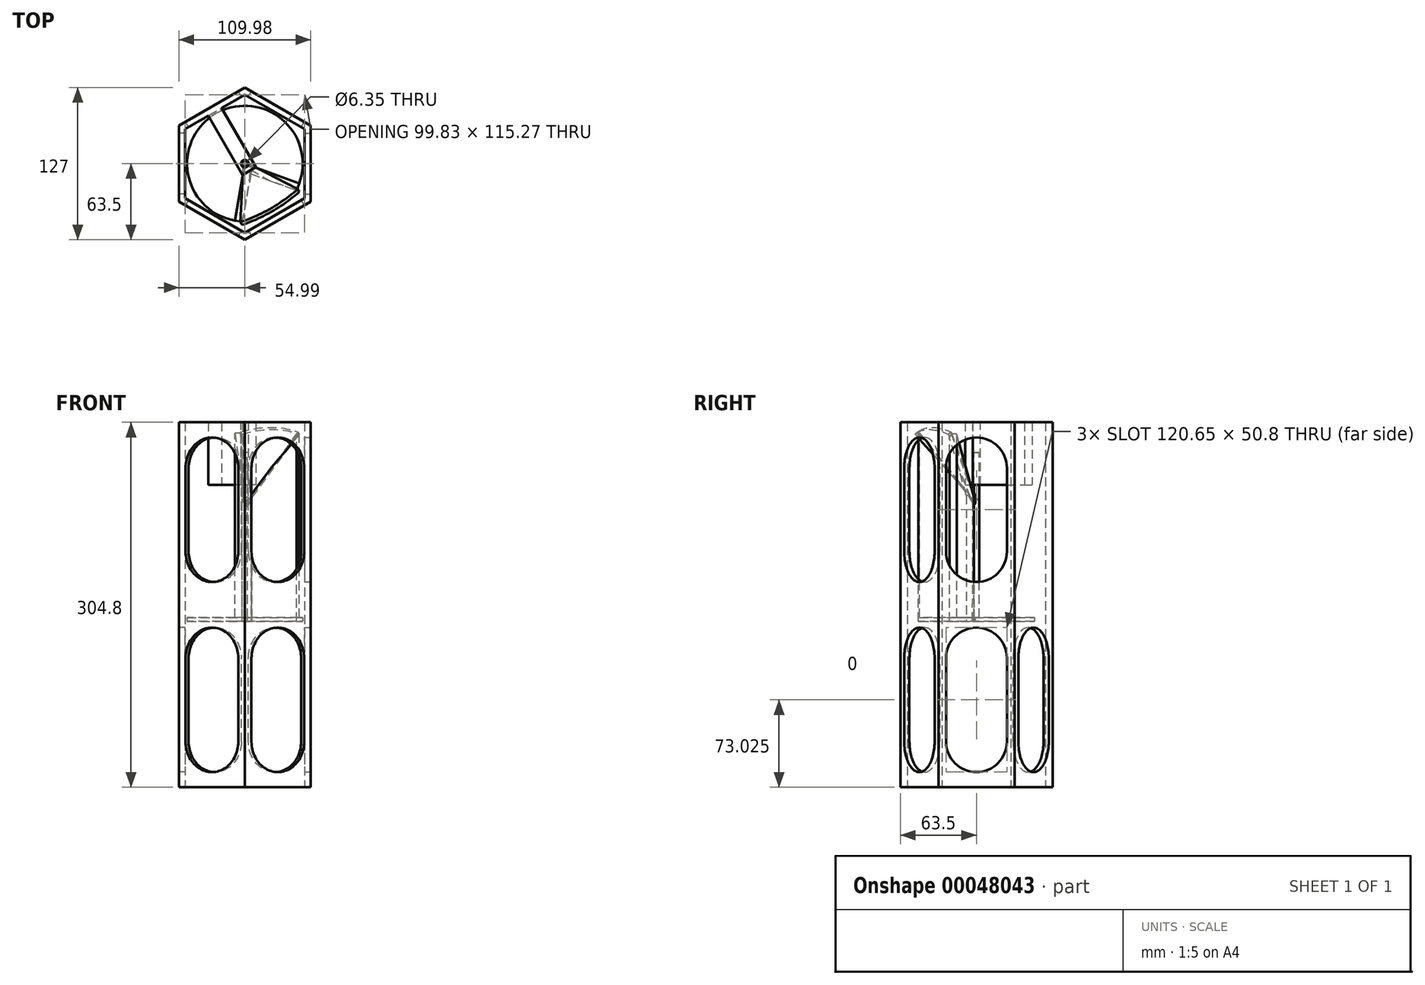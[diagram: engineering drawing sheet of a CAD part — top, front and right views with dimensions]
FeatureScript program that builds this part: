
annotation { "Feature Type Name" : "Feature", "Feature Type Description" : "" }
export const myFeature = defineFeature(function(context is Context, id is Id, definition is map)
    precondition{}
    {
        {
            var Q0;
            Q0=qCreatedBy(makeId("Top.planeOp"),FACE);
            var sketch = newSketch(context, id + "F0", { "sketchPlane" : qUnion([Q0])});
            skLineSegment(sketch, "E0", {"start": v(-55, 0) * mm, "end": v(-55, 31.75) * mm});
            skLineSegment(sketch, "E1", {"start": v(-55, 31.75) * mm, "end": v(0, 63.5) * mm});
            skLineSegment(sketch, "E2", {"start": v(0, 63.5) * mm, "end": v(55, 31.75) * mm});
            skLineSegment(sketch, "E3", {"start": v(55, 31.75) * mm, "end": v(55, 0) * mm});
            skLineSegment(sketch, "E4", {"start": v(55, 0) * mm, "end": v(55, -31.75) * mm});
            skLineSegment(sketch, "E5", {"start": v(55, -31.75) * mm, "end": v(0, -63.5) * mm});
            skLineSegment(sketch, "E6", {"start": v(0, -63.5) * mm, "end": v(-55, -31.75) * mm});
            skLineSegment(sketch, "E7", {"start": v(-55, -31.75) * mm, "end": v(-55, 0) * mm});
            skLineSegment(sketch, "E8.0", {"start": v(-49.91, 0) * mm, "end": v(-49.91, 28.82) * mm});
            skLineSegment(sketch, "E8.1", {"start": v(-49.91, -28.82) * mm, "end": v(-49.91, 0) * mm});
            skLineSegment(sketch, "E8.2", {"start": v(-49.91, 28.82) * mm, "end": v(0, 57.63) * mm});
            skLineSegment(sketch, "E8.3", {"start": v(0, -57.63) * mm, "end": v(-49.91, -28.82) * mm});
            skLineSegment(sketch, "E8.4", {"start": v(0, 57.63) * mm, "end": v(49.91, 28.82) * mm});
            skLineSegment(sketch, "E8.5", {"start": v(49.91, 28.82) * mm, "end": v(49.91, 0) * mm});
            skLineSegment(sketch, "E8.6", {"start": v(49.91, 0) * mm, "end": v(49.91, -28.82) * mm});
            skLineSegment(sketch, "E8.7", {"start": v(49.91, -28.82) * mm, "end": v(0, -57.63) * mm});
            skSolve(sketch);
        }
        {
            var Q0;
            Q0 = qSketchRegion(id + "F0", true);
            extrude(context, id + "F1", {"entities" : qUnion([Q0]), "depth" : 304.8 * mm});
        }
        {
            var Q0;
            Q0=makeQuery(id+"F1.opExtrude","SWEPT_FACE",FACE,{"disambiguationData":[OSD([sQuery(id+"F0.wireOp",EDGE,"E1")])]});
            var sketch = newSketch(context, id + "F2", { "sketchPlane" : qUnion([Q0])});
            skLineSegment(sketch, "E9", {"start": v(31.75, 152.4) * mm, "end": v(-31.75, 152.4) * mm, "construction": true});
            skSolve(sketch);
        }
        {
            var Q0;
            Q0=sQuery(id+"F2.wireOp",VERTEX,"E9.start");
            var Q1;
            Q1=sQuery(id+"F2.wireOp",VERTEX,"E9.end");
            var Q2;
            Q2=makeQuery(id+"F1.opExtrude","CAP_VERTEX",VERTEX,{"disambiguationData":[OSD([sQuery(id+"F0.wireOp",EDGE,"E8.3"),sQuery(id+"F0.wireOp",EDGE,"E8.7")])],"isStart":false});
            cPlane(context, id + "F3", {"entities" : qUnion([Q0, Q1, Q2]), "cplaneType" : CPlaneType.THREE_POINT, "offset" : 152.4 * mm, "width" : 152.4 * mm, "height" : 152.4 * mm});
        }
        {
            var Q0;
            Q0=makeQuery(id+"F1.opExtrude","CAP_VERTEX",VERTEX,{"disambiguationData":[OSD([sQuery(id+"F0.wireOp",EDGE,"E8.1"),sQuery(id+"F0.wireOp",EDGE,"E8.3")])],"isStart":false});
            var Q1;
            Q1=makeQuery(id+"F1.opExtrude","CAP_VERTEX",VERTEX,{"disambiguationData":[OSD([sQuery(id+"F0.wireOp",EDGE,"E8.4"),sQuery(id+"F0.wireOp",EDGE,"E8.5")])],"isStart":false});
            var Q2;
            Q2=makeQuery(id+"F1.opExtrude","CAP_VERTEX",VERTEX,{"disambiguationData":[OSD([sQuery(id+"F0.wireOp",EDGE,"E8.4"),sQuery(id+"F0.wireOp",EDGE,"E8.5")])],"isStart":true});
            cPlane(context, id + "F4", {"entities" : qUnion([Q0, Q1, Q2]), "cplaneType" : CPlaneType.THREE_POINT, "offset" : 152.4 * mm, "width" : 152.4 * mm, "height" : 152.4 * mm});
        }
        {
            var Q0;
            Q0=makeQuery(id+"F1.opExtrude","CAP_VERTEX",VERTEX,{"disambiguationData":[OSD([sQuery(id+"F0.wireOp",EDGE,"E8.0"),sQuery(id+"F0.wireOp",EDGE,"E8.2")])],"isStart":false});
            var Q1;
            Q1=makeQuery(id+"F1.opExtrude","CAP_VERTEX",VERTEX,{"disambiguationData":[OSD([sQuery(id+"F0.wireOp",EDGE,"E8.0"),sQuery(id+"F0.wireOp",EDGE,"E8.2")])],"isStart":true});
            var Q2;
            Q2=makeQuery(id+"F1.opExtrude","CAP_VERTEX",VERTEX,{"disambiguationData":[OSD([sQuery(id+"F0.wireOp",EDGE,"E8.6"),sQuery(id+"F0.wireOp",EDGE,"E8.7")])],"isStart":false});
            cPlane(context, id + "F5", {"entities" : qUnion([Q0, Q1, Q2]), "cplaneType" : CPlaneType.THREE_POINT, "offset" : 152.4 * mm, "width" : 152.4 * mm, "height" : 152.4 * mm});
        }
        {
            var Q0;
            Q0=qCreatedBy(id+"F3.planeOp",FACE);
            var sketch = newSketch(context, id + "F6", { "sketchPlane" : qUnion([Q0])});
            skLineSegment(sketch, "E10", {"start": v(-59.53, 181.84) * mm, "end": v(8.15, 204) * mm, "construction": true});
            skArc(sketch, "E11", {"start": v(-56.89, 262.57) * mm, "mid": v(-84.66, 258.6) * mm, "end": v(-109.4, 245.38) * mm});
            skLineSegment(sketch, "E12", {"start": v(-109.4, 245.38) * mm, "end": v(-59.53, 181.84) * mm});
            skLineSegment(sketch, "E13", {"start": v(-56.89, 262.57) * mm, "end": v(-59.53, 181.84) * mm});
            skLineSegment(sketch, "E14", {"start": v(-59.53, 181.84) * mm, "end": v(-95.11, 290.54) * mm, "construction": true});
            skSolve(sketch);
        }
        {
            var Q0;
            Q0 = qSketchRegion(id + "F6", true);
            extrude(context, id + "F7", {"entities" : qUnion([Q0]), "operationType" : NewBodyOperationType.ADD, "depth" : 3.17 * mm});
        }
        {
            var Q0;
            Q0=makeQuery(id+"F1.opExtrude","SWEPT_FACE",FACE,{"disambiguationData":[OSD([sQuery(id+"F0.wireOp",EDGE,"E8.2")])]});
            var sketch = newSketch(context, id + "F8", { "sketchPlane" : qUnion([Q0])});
            skLineSegment(sketch, "E15.bottom", {"start": v(-6.56, 304.8) * mm, "end": v(6.56, 304.8) * mm});
            skLineSegment(sketch, "E15.top", {"start": v(-6.56, 252.42) * mm, "end": v(6.56, 252.42) * mm});
            skLineSegment(sketch, "E15.left", {"start": v(-6.56, 304.8) * mm, "end": v(-6.56, 252.42) * mm});
            skLineSegment(sketch, "E15.right", {"start": v(6.56, 304.8) * mm, "end": v(6.56, 252.42) * mm});
            skLineSegment(sketch, "E16", {"start": v(0, 304.8) * mm, "end": v(0, 226.31) * mm, "construction": true});
            skPoint(sketch, "E16.endSnap0", {"position": v(0, 304.8) * mm});
            skSolve(sketch);
        }
        {
            var Q0;
            Q0 = qSketchRegion(id + "F8", true);
            extrude(context, id + "F9", {"entities" : qUnion([Q0]), "operationType" : NewBodyOperationType.ADD, "depth" : 57.15 * mm});
        }
        {
            var Q0;
            Q0=makeQuery(id+"F9.boolean.opBoolean","MERGE",FACE,{"derivedFrom":[makeQuery(id+"F1.opExtrude","CAP_FACE",FACE,{"disambiguationData":[OSD([sQuery(id+"F0.wireOp",EDGE,"E0"),sQuery(id+"F0.wireOp",EDGE,"E1"),sQuery(id+"F0.wireOp",EDGE,"E2"),sQuery(id+"F0.wireOp",EDGE,"E3"),sQuery(id+"F0.wireOp",EDGE,"E4"),sQuery(id+"F0.wireOp",EDGE,"E5"),sQuery(id+"F0.wireOp",EDGE,"E6"),sQuery(id+"F0.wireOp",EDGE,"E7"),sQuery(id+"F0.wireOp",EDGE,"E8.0"),sQuery(id+"F0.wireOp",EDGE,"E8.1"),sQuery(id+"F0.wireOp",EDGE,"E8.2"),sQuery(id+"F0.wireOp",EDGE,"E8.3"),sQuery(id+"F0.wireOp",EDGE,"E8.4"),sQuery(id+"F0.wireOp",EDGE,"E8.5"),sQuery(id+"F0.wireOp",EDGE,"E8.6"),sQuery(id+"F0.wireOp",EDGE,"E8.7")])],"isStart":false}),makeQuery(id+"F9.opExtrude","SWEPT_FACE",FACE,{"disambiguationData":[OSD([sQuery(id+"F8.wireOp",EDGE,"E15.bottom")])]})]});
            var sketch = newSketch(context, id + "F10", { "sketchPlane" : qUnion([Q0])});
            skCircle(sketch, "E17", {"center": v(0, 0) * mm, "radius": 3.18 * mm});
            skSolve(sketch);
        }
        {
            var Q0;
            Q0 = qSketchRegion(id + "F10", true);
            extrude(context, id + "F11", {"entities" : qUnion([Q0]), "operationType" : NewBodyOperationType.REMOVE, "endBound" : BoundingType.THROUGH_ALL, "oppositeDirection" : true, "depth" : 25.4 * mm});
        }
        {
            var Q0;
            Q0=makeQuery(id+"F9.boolean.opBoolean","MERGE",FACE,{"derivedFrom":[makeQuery(id+"F1.opExtrude","CAP_FACE",FACE,{"disambiguationData":[OSD([sQuery(id+"F0.wireOp",EDGE,"E0"),sQuery(id+"F0.wireOp",EDGE,"E1"),sQuery(id+"F0.wireOp",EDGE,"E2"),sQuery(id+"F0.wireOp",EDGE,"E3"),sQuery(id+"F0.wireOp",EDGE,"E4"),sQuery(id+"F0.wireOp",EDGE,"E5"),sQuery(id+"F0.wireOp",EDGE,"E6"),sQuery(id+"F0.wireOp",EDGE,"E7"),sQuery(id+"F0.wireOp",EDGE,"E8.0"),sQuery(id+"F0.wireOp",EDGE,"E8.1"),sQuery(id+"F0.wireOp",EDGE,"E8.2"),sQuery(id+"F0.wireOp",EDGE,"E8.3"),sQuery(id+"F0.wireOp",EDGE,"E8.4"),sQuery(id+"F0.wireOp",EDGE,"E8.5"),sQuery(id+"F0.wireOp",EDGE,"E8.6"),sQuery(id+"F0.wireOp",EDGE,"E8.7")])],"isStart":false}),makeQuery(id+"F9.opExtrude","SWEPT_FACE",FACE,{"disambiguationData":[OSD([sQuery(id+"F8.wireOp",EDGE,"E15.bottom")])]})]});
            var sketch = newSketch(context, id + "F12", { "sketchPlane" : qUnion([Q0])});
            skCircle(sketch, "E18", {"center": v(0, 0) * mm, "radius": 2.24 * mm});
            skSolve(sketch);
        }
        {
            var Q0;
            Q0 = qSketchRegion(id + "F12", true);
            extrude(context, id + "F13", {"entities" : qUnion([Q0]), "operationType" : NewBodyOperationType.ADD, "oppositeDirection" : true, "depth" : 166.25 * mm, "hasSecondDirection" : true, "secondDirectionOppositeDirection" : true, "secondDirectionDepth" : 25.4 * mm});
        }
        {
            var Q0;
            Q0=makeQuery(id+"F1.opExtrude","SWEPT_FACE",FACE,{"disambiguationData":[OSD([sQuery(id+"F0.wireOp",EDGE,"E3"),sQuery(id+"F0.wireOp",EDGE,"E4")])]});
            var sketch = newSketch(context, id + "F14", { "sketchPlane" : qUnion([Q0])});
            skLineSegment(sketch, "E19", {"start": v(-25.4, 266.7) * mm, "end": v(-25.4, 196.85) * mm});
            skLineSegment(sketch, "E20", {"start": v(25.4, 266.7) * mm, "end": v(25.4, 196.85) * mm});
            skArc(sketch, "E21", {"start": v(-25.4, 266.7) * mm, "mid": v(0, 292.1) * mm, "end": v(25.4, 266.7) * mm});
            skArc(sketch, "E22", {"start": v(-25.4, 196.85) * mm, "mid": v(0, 171.45) * mm, "end": v(25.4, 196.85) * mm});
            skLineSegment(sketch, "E23", {"start": v(0, 304.8) * mm, "end": v(0, 141.13) * mm, "construction": true});
            skPoint(sketch, "E23.endSnap0", {"position": v(0, 304.8) * mm});
            skLineSegment(sketch, "E24", {"start": v(-25.4, 107.95) * mm, "end": v(-25.4, 38.1) * mm});
            skArc(sketch, "E25", {"start": v(-25.4, 107.95) * mm, "mid": v(0, 133.35) * mm, "end": v(25.4, 107.95) * mm});
            skLineSegment(sketch, "E26", {"start": v(25.4, 107.95) * mm, "end": v(25.4, 38.1) * mm});
            skLineSegment(sketch, "E27", {"start": v(0, 160.02) * mm, "end": v(0, 0) * mm, "construction": true});
            skArc(sketch, "E28", {"start": v(-25.4, 38.1) * mm, "mid": v(0, 12.7) * mm, "end": v(25.4, 38.1) * mm});
            skSolve(sketch);
        }
        {
            var Q0;
            Q0 = qSketchRegion(id + "F14", true);
            extrude(context, id + "F15", {"entities" : qUnion([Q0]), "operationType" : NewBodyOperationType.REMOVE, "endBound" : BoundingType.UP_TO_NEXT, "oppositeDirection" : true, "depth" : 25.4 * mm});
        }
        {
            var Q0;
            Q0=makeQuery(id+"F1.opExtrude","SWEPT_FACE",FACE,{"disambiguationData":[OSD([sQuery(id+"F0.wireOp",EDGE,"E5")])]});
            var sketch = newSketch(context, id + "F16", { "sketchPlane" : qUnion([Q0])});
            skLineSegment(sketch, "E29", {"start": v(-25.4, 266.7) * mm, "end": v(-25.4, 196.85) * mm});
            skLineSegment(sketch, "E30", {"start": v(25.4, 266.7) * mm, "end": v(25.4, 196.85) * mm});
            skArc(sketch, "E31", {"start": v(-25.4, 196.85) * mm, "mid": v(0, 171.45) * mm, "end": v(25.4, 196.85) * mm});
            skArc(sketch, "E32", {"start": v(-25.4, 266.7) * mm, "mid": v(0, 292.1) * mm, "end": v(25.4, 266.7) * mm});
            skLineSegment(sketch, "E33", {"start": v(0, 304.8) * mm, "end": v(0, 180.72) * mm, "construction": true});
            skLineSegment(sketch, "E34", {"start": v(25.4, 107.95) * mm, "end": v(25.4, 38.1) * mm});
            skLineSegment(sketch, "E35", {"start": v(-25.4, 107.95) * mm, "end": v(-25.4, 38.1) * mm});
            skArc(sketch, "E36", {"start": v(-25.4, 38.1) * mm, "mid": v(0, 12.7) * mm, "end": v(25.4, 38.1) * mm});
            skArc(sketch, "E37", {"start": v(-25.4, 107.95) * mm, "mid": v(0, 133.35) * mm, "end": v(25.4, 107.95) * mm});
            skLineSegment(sketch, "E38", {"start": v(0, 138.62) * mm, "end": v(0, 0) * mm, "construction": true});
            skSolve(sketch);
        }
        {
            var Q0;
            Q0 = qSketchRegion(id + "F16", true);
            extrude(context, id + "F17", {"entities" : qUnion([Q0]), "operationType" : NewBodyOperationType.REMOVE, "endBound" : BoundingType.UP_TO_NEXT, "oppositeDirection" : true, "depth" : 25.4 * mm});
        }
        {
            var Q0;
            Q0=makeQuery(id+"F1.opExtrude","SWEPT_FACE",FACE,{"disambiguationData":[OSD([sQuery(id+"F0.wireOp",EDGE,"E6")])]});
            var sketch = newSketch(context, id + "F18", { "sketchPlane" : qUnion([Q0])});
            skLineSegment(sketch, "E39", {"start": v(-25.4, 266.7) * mm, "end": v(-25.4, 196.85) * mm});
            skLineSegment(sketch, "E40", {"start": v(25.4, 266.7) * mm, "end": v(25.4, 196.85) * mm});
            skArc(sketch, "E41", {"start": v(-25.4, 196.85) * mm, "mid": v(0, 171.45) * mm, "end": v(25.4, 196.85) * mm});
            skArc(sketch, "E42", {"start": v(-25.4, 266.7) * mm, "mid": v(0, 292.1) * mm, "end": v(25.4, 266.7) * mm});
            skLineSegment(sketch, "E43", {"start": v(0, 304.8) * mm, "end": v(0, 116.41) * mm, "construction": true});
            skLineSegment(sketch, "E44", {"start": v(-25.4, 107.95) * mm, "end": v(-25.4, 38.1) * mm});
            skArc(sketch, "E45", {"start": v(-25.4, 107.95) * mm, "mid": v(0, 133.35) * mm, "end": v(25.4, 107.95) * mm});
            skArc(sketch, "E46", {"start": v(-25.4, 38.1) * mm, "mid": v(0, 12.7) * mm, "end": v(25.4, 38.1) * mm});
            skLineSegment(sketch, "E47", {"start": v(0, 218.51) * mm, "end": v(0, 0) * mm, "construction": true});
            skLineSegment(sketch, "E48", {"start": v(25.4, 107.95) * mm, "end": v(25.4, 38.1) * mm});
            skSolve(sketch);
        }
        {
            var Q0;
            Q0 = qSketchRegion(id + "F18", true);
            extrude(context, id + "F19", {"entities" : qUnion([Q0]), "operationType" : NewBodyOperationType.REMOVE, "endBound" : BoundingType.UP_TO_NEXT, "oppositeDirection" : true, "depth" : 25.4 * mm});
        }
        {
            var Q0;
            Q0=makeQuery(id+"F13.opExtrude","CAP_FACE",FACE,{"disambiguationData":[OSD([sQuery(id+"F12.wireOp",EDGE,"E18")])],"isStart":false});
            var sketch = newSketch(context, id + "F20", { "sketchPlane" : qUnion([Q0])});
            skArc(sketch, "E49", {"start": v(45.35, 16.5) * mm, "mid": v(-24.13, -41.8) * mm, "end": v(-8.38, 47.53) * mm});
            skLineSegment(sketch, "E50", {"start": v(45.35, 16.5) * mm, "end": v(0, 0) * mm});
            skLineSegment(sketch, "E51", {"start": v(0, 0) * mm, "end": v(-8.38, 47.53) * mm});
            skLineSegment(sketch, "E52", {"start": v(0, 0) * mm, "end": v(18.43, 31.93) * mm, "construction": true});
            skLineSegment(sketch, "E53", {"start": v(0, 0) * mm, "end": v(0, 38.58) * mm, "construction": true});
            skSolve(sketch);
        }
        {
            var Q0;
            Q0 = qSketchRegion(id + "F20", true);
            extrude(context, id + "F21", {"entities" : qUnion([Q0]), "operationType" : NewBodyOperationType.ADD, "oppositeDirection" : true, "depth" : 3.17 * mm});
        }
        {
            var Q0;
            Q0=makeQuery(id+"F21.opExtrude","SWEPT_FACE",FACE,{"disambiguationData":[OSD([sQuery(id+"F20.wireOp",EDGE,"E51")])]});
            var sketch = newSketch(context, id + "F22", { "sketchPlane" : qUnion([Q0])});
            skLineSegment(sketch, "E54", {"start": v(-48.26, 138.55) * mm, "end": v(-48.26, 295.82) * mm});
            skLineSegment(sketch, "E55", {"start": v(-48.26, 295.82) * mm, "end": v(-1.9, 238.98) * mm});
            skLineSegment(sketch, "E56", {"start": v(-1.9, 238.98) * mm, "end": v(-2.24, 138.55) * mm});
            skLineSegment(sketch, "E57", {"start": v(-2.24, 138.55) * mm, "end": v(-48.26, 138.55) * mm});
            skSolve(sketch);
        }
        {
            var Q0;
            Q0 = qSketchRegion(id + "F22", true);
            extrude(context, id + "F23", {"entities" : qUnion([Q0]), "operationType" : NewBodyOperationType.ADD, "depth" : 6.35 * mm});
        }
        {
            var Q0;
            Q0=makeQuery(id+"F21.opExtrude","SWEPT_FACE",FACE,{"disambiguationData":[OSD([sQuery(id+"F20.wireOp",EDGE,"E50")])]});
            var sketch = newSketch(context, id + "F24", { "sketchPlane" : qUnion([Q0])});
            skLineSegment(sketch, "E58", {"start": v(48.26, 138.55) * mm, "end": v(48.26, 295.32) * mm});
            skLineSegment(sketch, "E59", {"start": v(48.26, 138.55) * mm, "end": v(6.44, 138.55) * mm});
            skLineSegment(sketch, "E60", {"start": v(6.44, 138.55) * mm, "end": v(6.44, 242.37) * mm});
            skLineSegment(sketch, "E61", {"start": v(6.44, 242.37) * mm, "end": v(48.26, 295.32) * mm});
            skSolve(sketch);
        }
        {
            var Q0;
            Q0 = qSketchRegion(id + "F24", true);
            extrude(context, id + "F25", {"entities" : qUnion([Q0]), "operationType" : NewBodyOperationType.ADD, "depth" : 6.35 * mm});
        }
        {
            var Q0;
            Q0=makeQuery(id+"F1.opExtrude","SWEPT_FACE",FACE,{"disambiguationData":[OSD([sQuery(id+"F0.wireOp",EDGE,"E2")])]});
            var sketch = newSketch(context, id + "F26", { "sketchPlane" : qUnion([Q0])});
            skPoint(sketch, "E62.endSnap0", {"position": v(0, 0) * mm});
            skLineSegment(sketch, "E63", {"start": v(-25.4, 107.95) * mm, "end": v(-25.4, 38.1) * mm});
            skLineSegment(sketch, "E64", {"start": v(25.4, 107.95) * mm, "end": v(25.4, 38.1) * mm});
            skArc(sketch, "E65", {"start": v(-25.4, 107.95) * mm, "mid": v(0, 133.35) * mm, "end": v(25.4, 107.95) * mm});
            skArc(sketch, "E66", {"start": v(-25.4, 38.1) * mm, "mid": v(0, 12.7) * mm, "end": v(25.4, 38.1) * mm});
            skLineSegment(sketch, "E67", {"start": v(0, 107.95) * mm, "end": v(0, 0) * mm, "construction": true});
            skSolve(sketch);
        }
        {
            var Q0;
            Q0 = qSketchRegion(id + "F26", true);
            extrude(context, id + "F27", {"entities" : qUnion([Q0]), "operationType" : NewBodyOperationType.REMOVE, "endBound" : BoundingType.UP_TO_NEXT, "oppositeDirection" : true, "depth" : 25.4 * mm});
        }
        {
            var Q0;
            {var subQ0=sQuery(id+"F0.wireOp",EDGE,"E1");Q0=makeQuery(id+"F2.imprint","IMPRINT",FACE,{"disambiguationData":[TD([[makeQuery(id+"F2.imprint","IMPRINT",EDGE,{"derivedFrom":makeQuery(id+"F1.opExtrude","CAP_EDGE",EDGE,{"disambiguationData":[OSD([subQ0])],"isStart":true})}),-1.0]])]});}
            var sketch = newSketch(context, id + "F28", { "sketchPlane" : qUnion([Q0])});
            skLineSegment(sketch, "E68", {"start": v(0, 107.95) * mm, "end": v(0, 0) * mm, "construction": true});
            skArc(sketch, "E69", {"start": v(-25.4, 38.1) * mm, "mid": v(0, 12.7) * mm, "end": v(25.4, 38.1) * mm});
            skArc(sketch, "E70", {"start": v(-25.4, 107.95) * mm, "mid": v(0, 133.35) * mm, "end": v(25.4, 107.95) * mm});
            skLineSegment(sketch, "E71", {"start": v(25.4, 107.95) * mm, "end": v(25.4, 38.1) * mm});
            skLineSegment(sketch, "E72", {"start": v(-25.4, 107.95) * mm, "end": v(-25.4, 38.1) * mm});
            skPoint(sketch, "E73.endSnap0", {"position": v(0, 0) * mm});
            skSolve(sketch);
        }
        {
            var Q0;
            Q0 = qSketchRegion(id + "F28", true);
            extrude(context, id + "F29", {"entities" : qUnion([Q0]), "operationType" : NewBodyOperationType.REMOVE, "endBound" : BoundingType.UP_TO_NEXT, "oppositeDirection" : true, "depth" : 25.4 * mm});
        }
        {
            var Q0;
            Q0=makeQuery(id+"F1.opExtrude","SWEPT_FACE",FACE,{"disambiguationData":[OSD([sQuery(id+"F0.wireOp",EDGE,"E0"),sQuery(id+"F0.wireOp",EDGE,"E7")])]});
            var sketch = newSketch(context, id + "F30", { "sketchPlane" : qUnion([Q0])});
            skLineSegment(sketch, "E74", {"start": v(0, 107.95) * mm, "end": v(0, 0) * mm, "construction": true});
            skArc(sketch, "E75", {"start": v(-25.4, 38.1) * mm, "mid": v(0, 12.7) * mm, "end": v(25.4, 38.1) * mm});
            skArc(sketch, "E76", {"start": v(-25.4, 107.95) * mm, "mid": v(0, 133.35) * mm, "end": v(25.4, 107.95) * mm});
            skLineSegment(sketch, "E77", {"start": v(25.4, 107.95) * mm, "end": v(25.4, 38.1) * mm});
            skLineSegment(sketch, "E78", {"start": v(-25.4, 107.95) * mm, "end": v(-25.4, 38.1) * mm});
            skPoint(sketch, "E79.endSnap0", {"position": v(0, 0) * mm});
            skSolve(sketch);
        }
        {
            var Q0;
            Q0 = qSketchRegion(id + "F30", true);
            extrude(context, id + "F31", {"entities" : qUnion([Q0]), "operationType" : NewBodyOperationType.REMOVE, "endBound" : BoundingType.UP_TO_NEXT, "oppositeDirection" : true, "depth" : 25.4 * mm});
        }
    });
